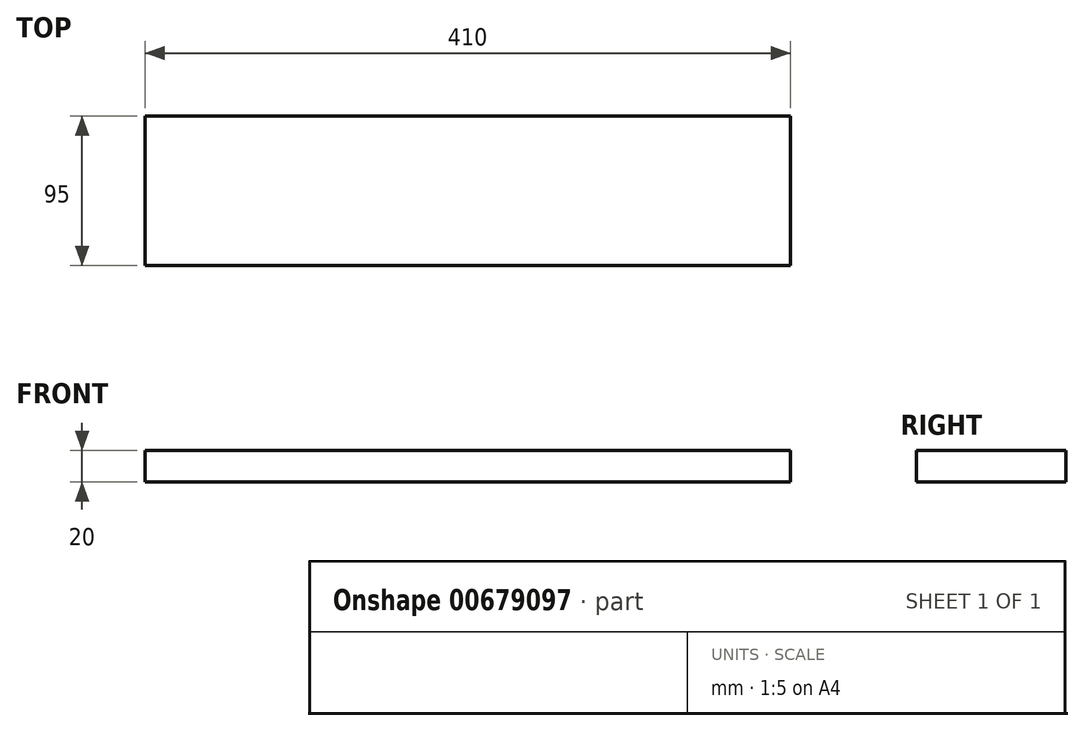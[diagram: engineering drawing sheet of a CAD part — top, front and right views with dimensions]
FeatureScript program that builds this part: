
annotation { "Feature Type Name" : "Feature", "Feature Type Description" : "" }
export const myFeature = defineFeature(function(context is Context, id is Id, definition is map)
    precondition{}
    {
        {
            var Q0;
            Q0=qCreatedBy(makeId("Right.planeOp"),FACE);
            var sketch = newSketch(context, id + "F0", { "sketchPlane" : qUnion([Q0])});
            skLineSegment(sketch, "E0.bottom", {"start": v(47.5, 10) * mm, "end": v(-47.5, 10) * mm});
            skLineSegment(sketch, "E0.top", {"start": v(47.5, -10) * mm, "end": v(-47.5, -10) * mm});
            skLineSegment(sketch, "E0.left", {"start": v(47.5, 10) * mm, "end": v(47.5, -10) * mm});
            skLineSegment(sketch, "E0.right", {"start": v(-47.5, 10) * mm, "end": v(-47.5, -10) * mm});
            skPoint(sketch, "E0.middle", {"position": v(0, 0) * mm});
            skSolve(sketch);
        }
        {
            var Q0;
            Q0 = qSketchRegion(id + "F0", true);
            extrude(context, id + "F1", {"entities" : qUnion([Q0]), "endBound" : BoundingType.SYMMETRIC, "depth" : 410 * mm, "offsetDistance" : 25 * mm});
        }
    });
